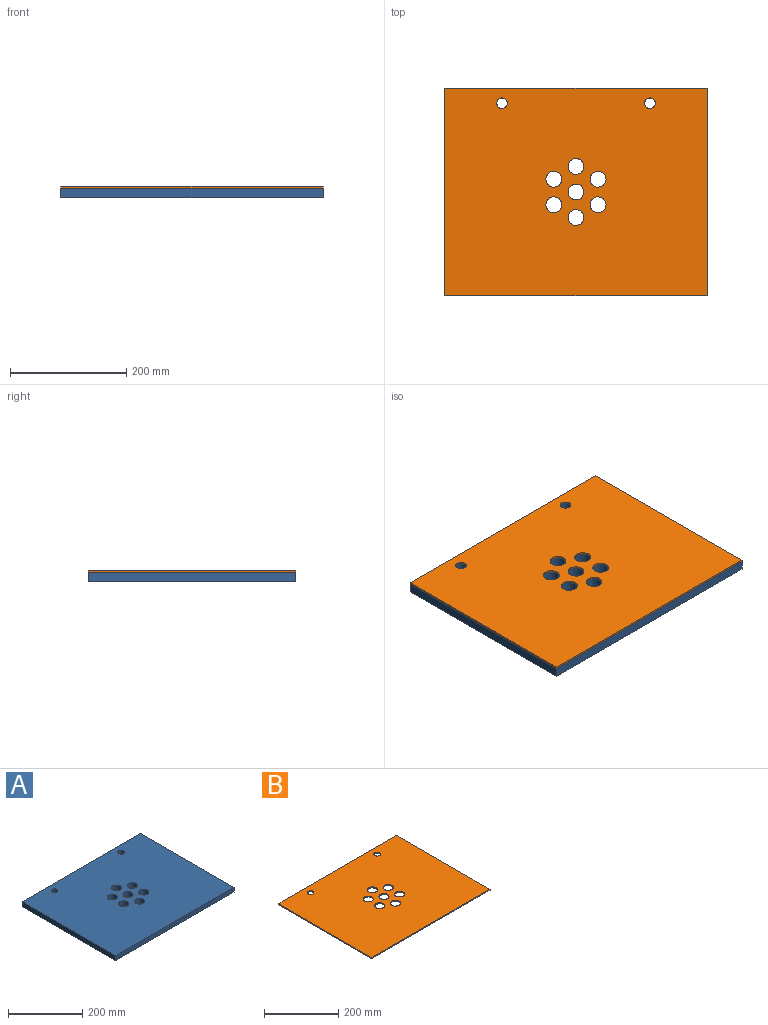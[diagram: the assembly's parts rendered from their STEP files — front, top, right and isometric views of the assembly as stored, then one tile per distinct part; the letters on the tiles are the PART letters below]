
ASSEMBLY  parts=2 mates=1
PART A: 15 faces, bbox 450.9x355.6x15.9 mm
  f0: plane 450.85x15.88mm, normal (0,1,0), area 7157.2mm2, adj f1,f12,f13,f14
  f1: plane 355.6x15.88mm, normal (1,0,0), area 5645.2mm2, adj f0,f2,f13,f14
  f2: plane 450.85x15.88mm, normal (0,-1,0), area 7157.2mm2, adj f1,f12,f13,f14
  f3: cylinder r=13.62mm len=27.23mm, axis (0,0,1), area 1358.2mm2, adj f13,f14
  f4: cylinder r=13.62mm len=27.23mm, axis (0,0,1), area 1358.2mm2, adj f13,f14
  f5: cylinder r=13.62mm len=27.23mm, axis (0,0,1), area 1358.2mm2, adj f13,f14
  f6: cylinder r=13.62mm len=27.23mm, axis (0,0,1), area 1358.2mm2, adj f13,f14
  f7: cylinder r=9.08mm len=18.16mm, axis (0,0,1), area 905.7mm2, adj f13,f14
  f8: cylinder r=9.08mm len=18.16mm, axis (0,0,1), area 905.7mm2, adj f13,f14
  f9: cylinder r=13.62mm len=27.23mm, axis (0,0,1), area 1358.2mm2, adj f13,f14
  f10: cylinder r=13.62mm len=27.23mm, axis (0,0,1), area 1358.2mm2, adj f13,f14
  f11: cylinder r=13.62mm len=27.23mm, axis (0,0,1), area 1358.2mm2, adj f13,f14
  f12: plane 355.6x15.88mm, normal (-1,0,0), area 5645.2mm2, adj f0,f2,f13,f14
  f13: plane 450.85x355.6mm, normal (0,0,-1), area 155726.6mm2, adj f0,f1,f2,f3,f4,f5,f6,f7
  f14: plane 450.85x355.6mm, normal (0,0,1), area 155726.6mm2, adj f0,f1,f2,f3,f4,f5,f6,f7
PART B: 15 faces, bbox 450.9x355.6x3.2 mm
  f0: plane 450.85x3.18mm, normal (0,1,0), area 1431.4mm2, adj f1,f12,f13,f14
  f1: plane 355.6x3.18mm, normal (-1,0,0), area 1129mm2, adj f0,f2,f13,f14
  f2: plane 450.85x3.18mm, normal (0,-1,0), area 1431.4mm2, adj f1,f12,f13,f14
  f3: cylinder r=13.62mm len=27.23mm, axis (0,0,-1), area 271.6mm2, adj f13,f14
  f4: cylinder r=13.62mm len=27.23mm, axis (0,0,-1), area 271.6mm2, adj f13,f14
  f5: cylinder r=13.62mm len=27.23mm, axis (0,0,-1), area 271.6mm2, adj f13,f14
  f6: cylinder r=13.62mm len=27.23mm, axis (0,0,-1), area 271.6mm2, adj f13,f14
  f7: cylinder r=9.08mm len=18.16mm, axis (0,0,-1), area 181.1mm2, adj f13,f14
  f8: cylinder r=9.08mm len=18.16mm, axis (0,0,-1), area 181.1mm2, adj f13,f14
  f9: cylinder r=13.62mm len=27.23mm, axis (0,0,-1), area 271.6mm2, adj f13,f14
  f10: cylinder r=13.62mm len=27.23mm, axis (0,0,-1), area 271.6mm2, adj f13,f14
  f11: cylinder r=13.62mm len=27.23mm, axis (0,0,-1), area 271.6mm2, adj f13,f14
  f12: plane 355.6x3.18mm, normal (1,0,0), area 1129mm2, adj f0,f2,f13,f14
  f13: plane 450.85x355.6mm, normal (0,0,1), area 155726.6mm2, adj f0,f1,f2,f3,f4,f5,f6,f7
  f14: plane 450.85x355.6mm, normal (0,0,-1), area 155726.6mm2, adj f0,f1,f2,f3,f4,f5,f6,f7
PLACE A t=(1.27,0.79,-1.5)mm
PLACE B t=(1.27,0.79,-1.5)mm fixed
MATE fastened A.f14 <-> B.f14  axis (0,0,1) through (1.27,0.28,-1.5)mm
